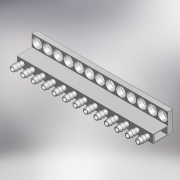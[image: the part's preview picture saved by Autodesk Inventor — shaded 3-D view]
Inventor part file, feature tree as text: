
AUTODESK INVENTOR PART (.ipt)
format: ipt  version: 2018 (Build 220112000, 112)  size: 313,344 bytes
history: native  units: in
note: dims shown in document units (in); Inventor stores cm internally (conversion verified against a paired STEP export)
features: other x8, extrude x5, pattern_linear x3, sketch x2, projected_geometry x1
ambient origin geometry x8: Origin, YZ Plane, XZ Plane, XY Plane, X Axis, Y Axis, Z Axis, Center Point
bodies: Body1 (feature_tree)
feature tree (19):
  other  "ManifoldExtension2.ipt"
  other  "CrossSection1"
  other  "Silicone Fitting Plane"
  other  "Cap Plane"
  other  "Base Sketch"
  extrude  "Base"  Depth=0.0591in
  extrude  "Extrusion21"  Depth=0.0591in
  other  "Silicone Fitting"
  extrude  "Airflow Cut"  Depth=0.4134in
  pattern_linear  "Airflow Cut Repetition"  Spacing1=0.5906in  [1 undecoded]
  pattern_linear  "Rectangular Pattern7"  Spacing1=-0.2067in  [1 undecoded]
  extrude  "Extrusion22"  TaperAngle=0.0deg  [1 undecoded]
  pattern_linear  "Rectangular Pattern8"  Spacing1=90.0deg  [1 undecoded]
  extrude  "Extrusion24"  Depth=0.1181in TaperAngle=0.0deg
  other  "Silicone Fitting Sketch"
  other  "Airflow Cut Sketch"
  projected_geometry  "Projected Loop7"
  sketch  "Sketch22"  dims[d87=0.0197in d88=0.0787in d89=-1.0625in d90=0.7874in d1=0.0591in]
  sketch  "Sketch23"  dims[d2=0.0591in d3=0.0591in d4=0.0197in d5=0.5906in d6=-0.2067in d8=0.0in d111=90.0deg d112=0.1181in d9=0.0in d12=-5.374in d155=5.1181in d157=0.4134in d158=5.1181in d160=0.4134in d161=5.374in d162=0.1969in d163=0.3214in d164=0.0in d165=0.4724in d166=0.0in d167=0.3937in d168=0.2067in d169=0.2362in d170=0.3937in d171=0.0in d172=5.1181in d174=0.4134in d181=0.0295in d182=0.0295in d183=0.0591in d184=0.0295in d185=0.4134in d186=0.0in]
note: 4 required parameter values undecoded (feature->parameter linkage not recoverable at this tier; creation-order binding heuristic only, values carry confidence <= 0.55)
